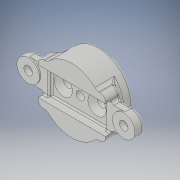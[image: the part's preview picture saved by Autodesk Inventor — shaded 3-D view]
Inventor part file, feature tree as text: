
AUTODESK INVENTOR PART (.ipt)
format: ipt  version: 2019.4 (Build 234330000, 330)  size: 647,168 bytes
history: native  units: mm
features: sketch x24, extrude x21, fillet x8, projected_geometry x7, chamfer x2, hole x2, pattern_circular x2, revolve x1, plane x1
ambient origin geometry x8: Origin, YZ Plane, XZ Plane, XY Plane, X Axis, Y Axis, Z Axis, Center Point
bodies: Solid1 (feature_tree)
feature tree (68):
  extrude  "Extrusion1"  Depth=1.0mm
  revolve  "Revolution1"  [1 undecoded]
  extrude  "Extrusion2"  Depth=4.0mm
  chamfer  "Chamfer1"  Distance=8.0mm
  extrude  "Extrusion6"  Depth=0.5mm TaperAngle=45.0deg
  extrude  "Extrusion7"  Depth=2.0mm TaperAngle=0.0deg
  extrude  "Extrusion8"  Depth=4.0mm TaperAngle=0.0deg
  extrude  "Extrusion9"  Depth=8.0mm
  extrude  "Extrusion10"  Depth=8.0mm
  extrude  "Extrusion11"  Depth=1.5mm TaperAngle=0.0deg
  fillet  "Fillet7"  [1 undecoded]
  extrude  "Extrusion13"  Depth=3.0mm TaperAngle=0.0deg
  extrude  "Extrusion14"  Depth=15.0mm
  fillet  "Fillet9"  Radius=3.0mm
  extrude  "Extrusion15"  Depth=3.0mm TaperAngle=0.0deg
  extrude  "Extrusion16"  Depth=3.0mm TaperAngle=0.0deg
  extrude  "Extrusion17"  Depth=9.0mm
  fillet  "Fillet10"  Radius=5.5mm
  fillet  "Fillet11"  Radius=6.0mm
  plane  "Work Plane1"
  extrude  "Extrusion18"  Depth=2.5mm TaperAngle=0.0deg
  extrude  "Extrusion19"  Depth=1.0mm
  hole  "Hole2"  [1 undecoded]
  pattern_circular  "Circular Pattern1"  Count=2 Angle=360.0deg
  chamfer  "Chamfer4"  Distance=1.0mm Angle=45.0deg
  extrude  "Extrusion20"  Depth=0.5mm TaperAngle=0.0deg
  extrude  "Extrusion22"  Depth=0.5mm
  extrude  "Extrusion24"  Depth=0.5mm TaperAngle=0.0deg
  extrude  "Extrusion25"  Depth=0.5mm TaperAngle=0.0deg
  extrude  "Extrusion26"  Depth=0.5mm
  fillet  "Fillet13"  Radius=23.0mm
  hole  "Hole4"  [1 undecoded]
  pattern_circular  "Circular Pattern3"  [2 undecoded]
  fillet  "Fillet14"  Radius=5.4mm
  fillet  "Fillet15"  Radius=23.0mm
  extrude  "Extrusion27"  Depth=0.5mm TaperAngle=0.0deg
  fillet  "Fillet16"  Radius=2.0mm
  sketch  "Sketch1"  dims[d0=3.0mm d1=1.0mm]
  sketch  "Sketch2"  dims[d2=19.95mm d3=14.0mm d4=0.0mm]
  sketch  "Sketch3"  dims[d5=3.0mm d6=4.0mm]
  projected_geometry  "Projected Loop1"
  sketch  "Sketch7"  dims[d7=4.0mm]
  sketch  "Sketch8"  dims[d8=90.0deg]
  sketch  "Sketch9"  dims[d10=19.95mm d11=8.0mm d12=0.0mm]
  sketch  "Sketch10"  dims[d13=1.0mm d18=0.5mm d19=2.0mm d20=45.0deg]
  projected_geometry  "Projected Loop2"
  sketch  "Sketch12"  dims[d33=15.0mm d34=2.0mm d35=0.0mm]
  sketch  "Sketch13"  dims[d36=11.95mm d37=4.0mm d38=0.0mm]
  sketch  "Sketch16"  dims[d39=34.0mm d40=8.0mm]
  projected_geometry  "Projected Loop3"
  sketch  "Sketch17"  dims[d41=2.0mm d42=0.0mm d43=8.0mm]
  sketch  "Sketch18"  dims[d44=8.0mm d45=1.5mm d46=0.0mm d58=0.0mm]
  sketch  "Sketch19"  dims[d59=23.0mm d60=3.0mm d61=0.0mm]
  projected_geometry  "Projected Loop4"
  sketch  "Sketch20"  dims[d63=24.0mm d64=15.0mm d65=3.0mm d66=0.0mm]
  sketch  "Sketch21"  dims[d68=2.0mm d74=3.0mm d75=0.0mm]
  sketch  "Sketch22"  dims[d76=10.1mm d77=3.0mm d78=0.0mm]
  sketch  "Sketch23"  dims[d79=2.0mm d80=9.0mm d81=5.5mm d82=0.0mm d83=6.0mm]
  sketch  "Sketch24"  dims[d84=3.0mm d85=0.0mm d86=2.5mm d87=0.0mm]
  projected_geometry  "Projected Loop5"
  sketch  "Sketch26"  dims[d88=1.0mm d89=1.0mm]
  sketch  "Sketch28"  dims[d90=11.0mm d91=0.0mm d92=0.0mm]
  projected_geometry  "Projected Loop8"
  sketch  "Sketch30"  dims[d93=5.0mm]
  sketch  "Sketch31"  dims[d94=5.0mm d95=0.0mm]
  sketch  "Sketch32"  dims[d96=3.0mm]
  sketch  "Sketch33"  dims[d97=6.0mm d98=3.1mm d99=6.0mm d100=6.5mm d101=2.0mm d102=90.0deg d103=10.0mm d104=0.0mm d105=20.0mm d106=360.0deg d108=1.0mm d109=2.0mm d110=45.0deg d111=5.4mm d112=0.0mm d116=23.0mm d117=5.4mm d118=0.0mm d121=5.4mm d122=0.0mm d123=23.0mm d135=23.0mm d136=19.98mm d137=1.0mm d138=5.4mm d139=0.0mm d140=23.0mm d141=5.4mm d142=0.0mm d143=2.0mm d144=3.0mm d145=3.1mm d146=6.0mm d147=6.5mm d148=2.0mm d149=90.0deg d150=10.0mm d151=0.0mm d152=20.0mm d153=360.0deg d155=1.0mm d156=1.0mm d157=20.0mm d158=0.0mm d159=1.0mm d160=0.0mm d161=0.5mm]
  projected_geometry  "Projected Loop9"
note: 6 required parameter values undecoded (feature->parameter linkage not recoverable at this tier; creation-order binding heuristic only, values carry confidence <= 0.55)